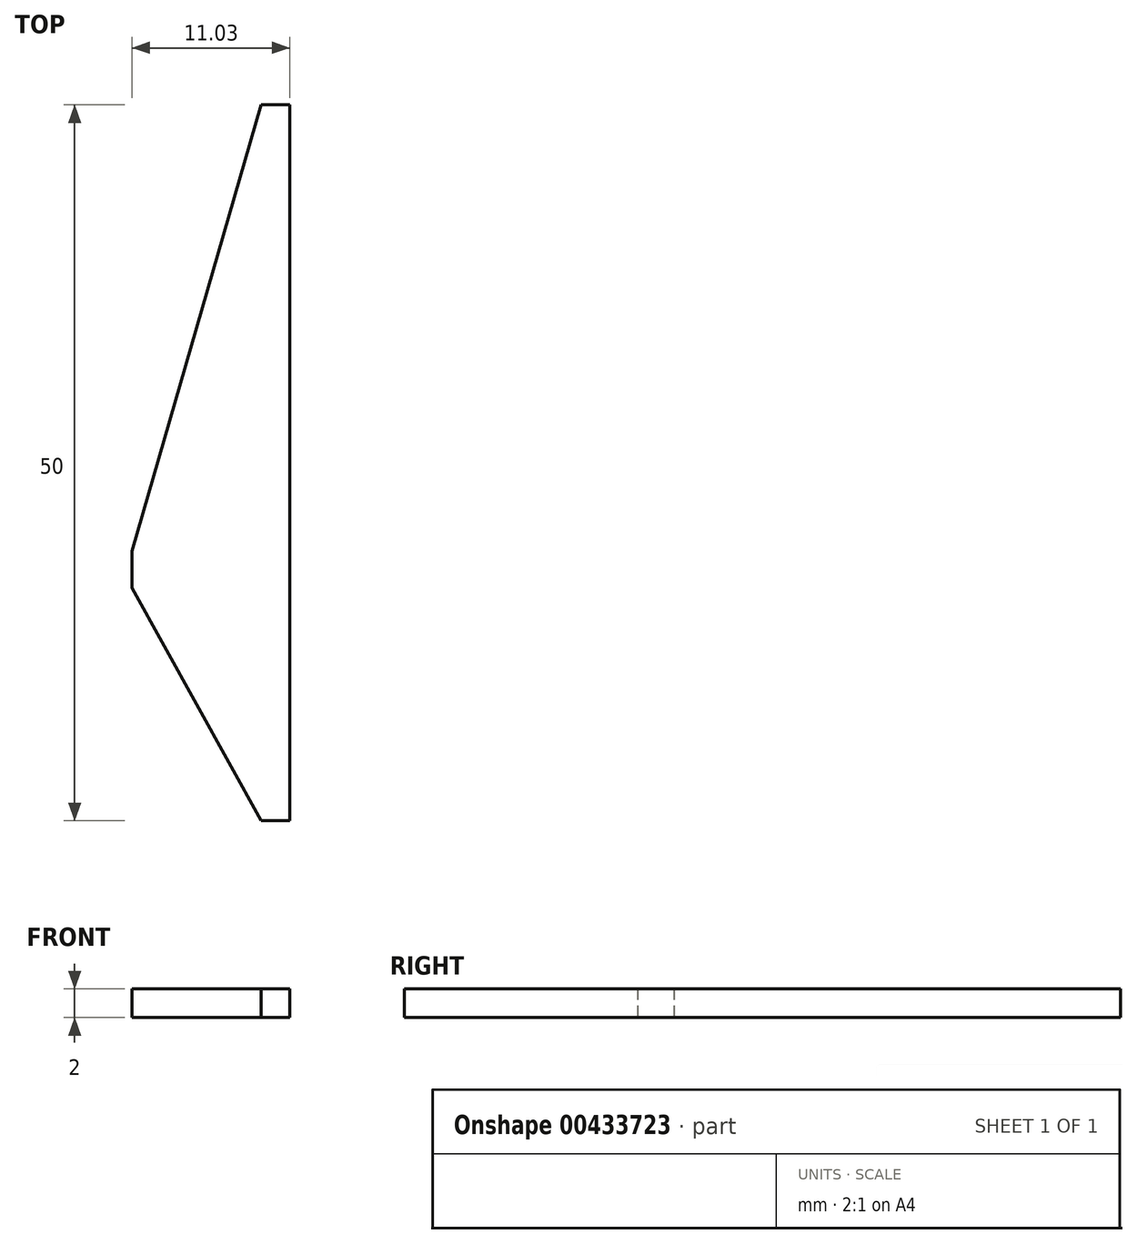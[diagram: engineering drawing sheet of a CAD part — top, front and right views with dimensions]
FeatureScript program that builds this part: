
annotation { "Feature Type Name" : "Feature", "Feature Type Description" : "" }
export const myFeature = defineFeature(function(context is Context, id is Id, definition is map)
    precondition{}
    {
        {
            var Q0;
            Q0=qCreatedBy(makeId("Top.planeOp"),FACE);
            var sketch = newSketch(context, id + "F0", { "sketchPlane" : qUnion([Q0])});
            skLineSegment(sketch, "E0", {"start": v(1.18, -17.76) * mm, "end": v(-0.83, -17.76) * mm});
            skLineSegment(sketch, "E1", {"start": v(-0.83, -17.76) * mm, "end": v(-9.85, -1.5) * mm});
            skLineSegment(sketch, "E2", {"start": v(-9.85, -1.5) * mm, "end": v(-9.85, 1.06) * mm});
            skLineSegment(sketch, "E3", {"start": v(-9.85, 1.06) * mm, "end": v(-0.83, 32.24) * mm});
            skLineSegment(sketch, "E4", {"start": v(-0.83, 32.24) * mm, "end": v(1.18, 32.24) * mm});
            skLineSegment(sketch, "E5", {"start": v(1.18, 32.24) * mm, "end": v(1.18, -17.76) * mm});
            skSolve(sketch);
        }
        {
            var Q0;
            Q0 = qSketchRegion(id + "F0", true);
            extrude(context, id + "F1", {"entities" : qUnion([Q0]), "depth" : 2 * mm, "offsetDistance" : 25.4 * mm});
        }
    });
